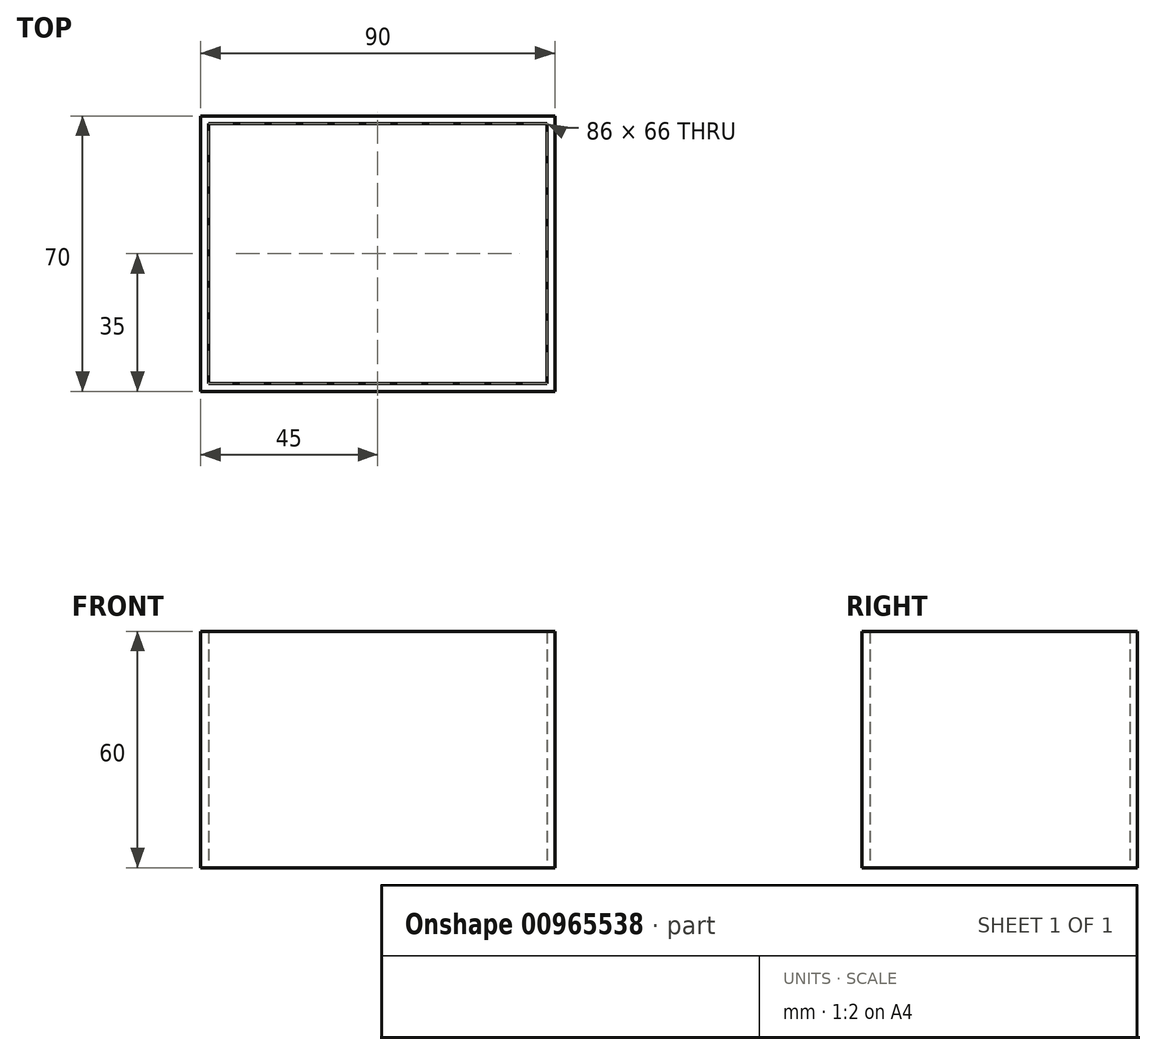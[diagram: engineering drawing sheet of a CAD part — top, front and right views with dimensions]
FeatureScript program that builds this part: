
annotation { "Feature Type Name" : "Feature", "Feature Type Description" : "" }
export const myFeature = defineFeature(function(context is Context, id is Id, definition is map)
    precondition{}
    {
        {
            var Q0;
            Q0=qCreatedBy(makeId("Top.planeOp"),FACE);
            var sketch = newSketch(context, id + "F0", { "sketchPlane" : qUnion([Q0])});
            skLineSegment(sketch, "E0.bottom", {"start": v(45, 35) * mm, "end": v(-45, 35) * mm});
            skLineSegment(sketch, "E0.top", {"start": v(45, -35) * mm, "end": v(-45, -35) * mm});
            skLineSegment(sketch, "E0.left", {"start": v(45, 35) * mm, "end": v(45, -35) * mm});
            skLineSegment(sketch, "E0.right", {"start": v(-45, 35) * mm, "end": v(-45, -35) * mm});
            skPoint(sketch, "E0.middle", {"position": v(0, 0) * mm});
            skLineSegment(sketch, "E1.bottom", {"start": v(43, -33) * mm, "end": v(-43, -33) * mm});
            skLineSegment(sketch, "E1.top", {"start": v(43, 33) * mm, "end": v(-43, 33) * mm});
            skLineSegment(sketch, "E1.left", {"start": v(43, -33) * mm, "end": v(43, 33) * mm});
            skLineSegment(sketch, "E1.right", {"start": v(-43, -33) * mm, "end": v(-43, 33) * mm});
            skSolve(sketch);
        }
        {
            var Q0;
            Q0=makeQuery(id+"F0.imprint","IMPRINT",FACE,{"disambiguationData":[TD([[makeQuery(id+"F0.imprint","IMPRINT",EDGE,{"derivedFrom":sQuery(id+"F0.wireOp",EDGE,"E0.bottom")}),1.0]])]});
            extrude(context, id + "F1", {"entities" : qUnion([Q0]), "depth" : 60 * mm, "offsetDistance" : 25 * mm});
        }
    });
